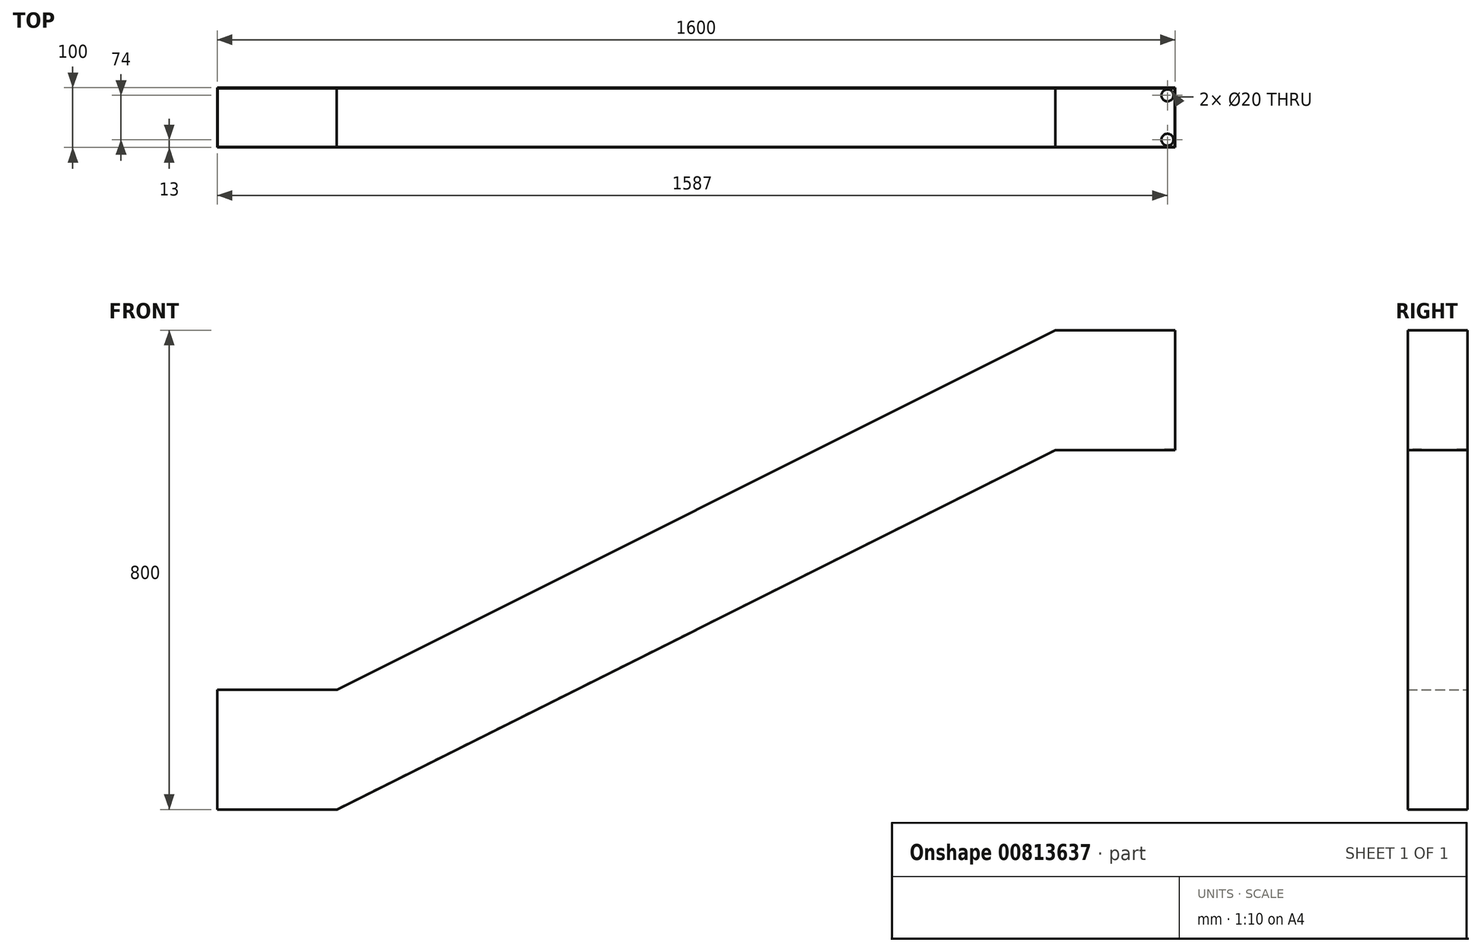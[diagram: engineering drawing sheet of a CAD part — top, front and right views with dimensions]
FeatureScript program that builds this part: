
annotation { "Feature Type Name" : "Feature", "Feature Type Description" : "" }
export const myFeature = defineFeature(function(context is Context, id is Id, definition is map)
    precondition{}
    {
        {
            var Q0;
            Q0=qCreatedBy(makeId("Front.planeOp"),FACE);
            var sketch = newSketch(context, id + "F0", { "sketchPlane" : qUnion([Q0])});
            skLineSegment(sketch, "E0", {"start": v(0, 0) * mm, "end": v(200, 0) * mm});
            skLineSegment(sketch, "E1", {"start": v(200, 0) * mm, "end": v(1400, 600) * mm});
            skLineSegment(sketch, "E2", {"start": v(1400, 600) * mm, "end": v(1600, 600) * mm});
            skLineSegment(sketch, "E3.0", {"start": v(1400, 800) * mm, "end": v(1600, 800) * mm});
            skLineSegment(sketch, "E4.0", {"start": v(0, 200) * mm, "end": v(200, 200) * mm});
            skLineSegment(sketch, "E5", {"start": v(1600, 800) * mm, "end": v(1600, 600) * mm});
            skLineSegment(sketch, "E6", {"start": v(0, 200) * mm, "end": v(0, 0) * mm});
            skLineSegment(sketch, "E7", {"start": v(1400, 800) * mm, "end": v(200, 200) * mm});
            skSolve(sketch);
        }
        {
            var Q0;
            Q0=makeQuery(id+"F0.imprint","IMPRINT",FACE,{"disambiguationData":[TD([[makeQuery(id+"F0.imprint","IMPRINT",EDGE,{"derivedFrom":sQuery(id+"F0.wireOp",EDGE,"E0")}),1.0]])]});
            extrude(context, id + "F1", {"entities" : qUnion([Q0]), "depth" : 100 * mm, "offsetDistance" : 25 * mm});
        }
        {
            var Q0;
            Q0=makeQuery(id+"F1.opExtrude","SWEPT_FACE",FACE,{"disambiguationData":[OSD([sQuery(id+"F0.wireOp",EDGE,"E4.0")])]});
            var Q1;
            Q1=makeQuery(id+"F1.opExtrude","SWEPT_FACE",FACE,{"disambiguationData":[OSD([sQuery(id+"F0.wireOp",EDGE,"E3.0")])]});
            var Q2;
            Q2=makeQuery(id+"F1.opExtrude","SWEPT_FACE",FACE,{"disambiguationData":[OSD([sQuery(id+"F0.wireOp",EDGE,"E7")])]});
            shell(context, id + "F2", {"entities" : qUnion([Q0, Q1, Q2]), "thickness" : 1 * mm});
        }
        {
            var Q0;
            Q0=makeQuery(id+"F2.opShell","OFFSET_FACE",FACE,{"disambiguationData":[OSD([sQuery(id+"F0.wireOp",EDGE,"E2")])]});
            var sketch = newSketch(context, id + "F3", { "sketchPlane" : qUnion([Q0])});
            skCircle(sketch, "E8", {"center": v(1587, -13) * mm, "radius": 12 * mm});
            skCircle(sketch, "E9.0", {"center": v(1587, -13) * mm, "radius": 10 * mm});
            skCircle(sketch, "E10", {"center": v(1587, -87) * mm, "radius": 12 * mm});
            skCircle(sketch, "E11.0", {"center": v(1587, -87) * mm, "radius": 10 * mm});
            skSolve(sketch);
        }
        {
            var Q0;
            Q0=sQuery(id+"F3.wireOp",EDGE,"E9.0");
            var Q1;
            Q1=sQuery(id+"F3.wireOp",EDGE,"E8");
            var Q2;
            Q2=sQuery(id+"F3.wireOp",EDGE,"E11.0");
            var Q3;
            Q3=sQuery(id+"F3.wireOp",EDGE,"E10");
            extrude(context, id + "F4", {"bodyType" : ToolBodyType.SURFACE, "surfaceEntities" : qUnion([Q0, Q1, Q2, Q3]), "depth" : 200 * mm, "offsetDistance" : 25 * mm});
        }
        {
            var Q0;
            Q0=sQuery(id+"F3.wireOp",VERTEX,"E8.center");
            var Q1;
            Q1=sQuery(id+"F3.wireOp",VERTEX,"E11.0.center");
            var Q2;
            Q2=makeQuery(id+"F1.opExtrude","SWEPT_BODY",BODY,{"disambiguationData":[OSD([sQuery(id+"F0.wireOp",EDGE,"E0"),sQuery(id+"F0.wireOp",EDGE,"E1"),sQuery(id+"F0.wireOp",EDGE,"E2"),sQuery(id+"F0.wireOp",EDGE,"E3.0"),sQuery(id+"F0.wireOp",EDGE,"E4.0"),sQuery(id+"F0.wireOp",EDGE,"b94ed2f5-d693-429c-bf34-7d5d2d5847e0"),sQuery(id+"F0.wireOp",EDGE,"E5"),sQuery(id+"F0.wireOp",EDGE,"E6")])]});
            hole(context, id + "F5", {"style" : HoleStyle.SIMPLE, "endStyle" : HoleEndStyle.THROUGH, "holeDiameter" : 20 * mm, "majorDiameter" : 5 * mm, "isTappedThrough" : true, "tappedDepth" : 12 * mm, "tapClearance" : 3, "locations" : qUnion([Q0, Q1]), "scope" : qUnion([Q2])});
        }
        {
            var Q0;
            Q0=makeQuery(id+"F1.opExtrude","SWEPT_FACE",FACE,{"disambiguationData":[OSD([sQuery(id+"F0.wireOp",EDGE,"E0")])]});
            var sketch = newSketch(context, id + "F6", { "sketchPlane" : qUnion([Q0])});
            skCircle(sketch, "E12", {"center": v(12, 88) * mm, "radius": 12 * mm});
            skCircle(sketch, "E13", {"center": v(12, 12) * mm, "radius": 12 * mm});
            skCircle(sketch, "E14.0", {"center": v(12, 12) * mm, "radius": 10 * mm});
            skCircle(sketch, "E15.0", {"center": v(12, 88) * mm, "radius": 10 * mm});
            skSolve(sketch);
        }
        {
            var Q0;
            Q0=sQuery(id+"F6.wireOp",EDGE,"E15.0");
            var Q1;
            Q1=sQuery(id+"F6.wireOp",EDGE,"E12");
            var Q2;
            Q2=sQuery(id+"F6.wireOp",EDGE,"E14.0");
            var Q3;
            Q3=sQuery(id+"F6.wireOp",EDGE,"E13");
            extrude(context, id + "F7", {"bodyType" : ToolBodyType.SURFACE, "surfaceEntities" : qUnion([Q0, Q1, Q2, Q3]), "oppositeDirection" : true, "depth" : 200 * mm, "offsetDistance" : 25 * mm});
        }
    });
